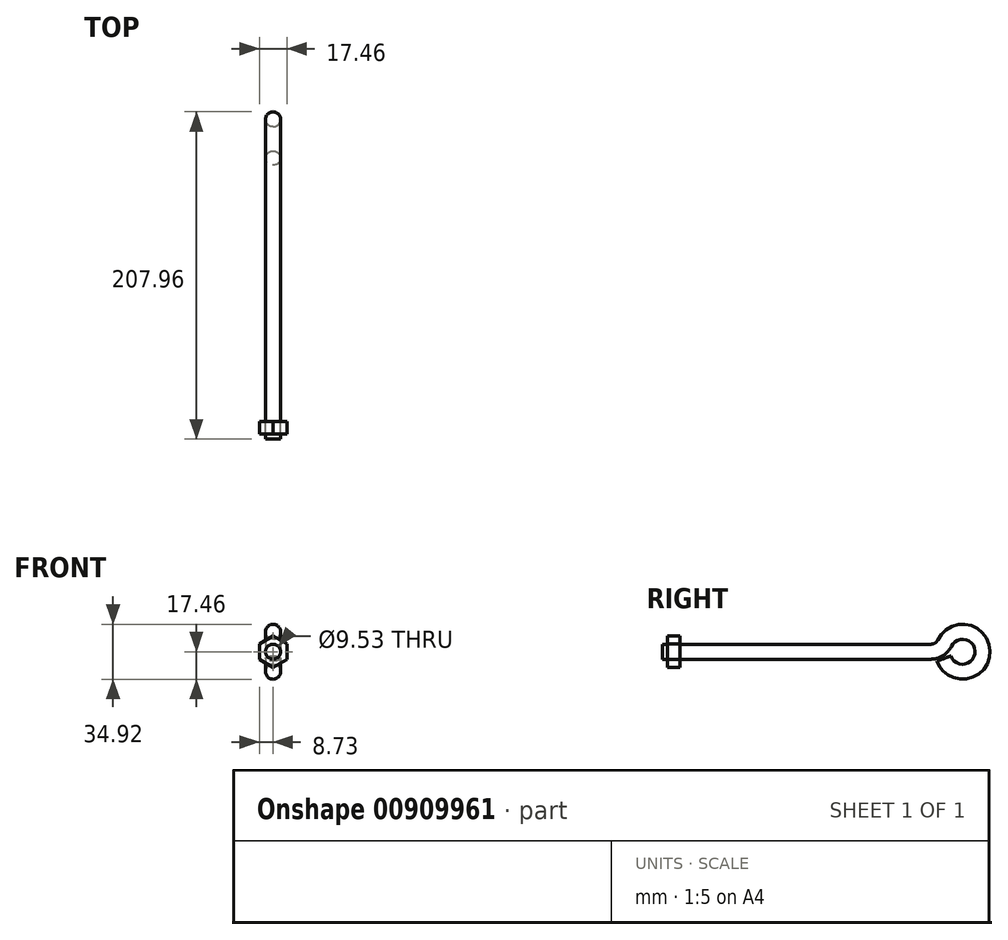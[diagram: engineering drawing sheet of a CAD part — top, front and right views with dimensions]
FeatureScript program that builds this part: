
annotation { "Feature Type Name" : "Feature", "Feature Type Description" : "" }
export const myFeature = defineFeature(function(context is Context, id is Id, definition is map)
    precondition{}
    {
        {
            var Q0;
            Q0=qCreatedBy(makeId("Right.planeOp"),FACE);
            var sketch = newSketch(context, id + "F0", { "sketchPlane" : qUnion([Q0])});
            skLineSegment(sketch, "E0", {"start": v(0, 0) * mm, "end": v(170.42, 0) * mm});
            skArc(sketch, "E1", {"start": v(170.42, 0) * mm, "mid": v(175.51, 1.47) * mm, "end": v(179.03, 5.44) * mm});
            skArc(sketch, "E2", {"start": v(178.57, -4.34) * mm, "mid": v(203.19, -0.6) * mm, "end": v(179.03, 5.44) * mm});
            skLineSegment(sketch, "E3", {"start": v(190.5, 0) * mm, "end": v(178.57, -4.34) * mm, "construction": true});
            skSolve(sketch);
        }
        {
            var Q0;
            Q0=qCreatedBy(makeId("Front.planeOp"),FACE);
            var sketch = newSketch(context, id + "F1", { "sketchPlane" : qUnion([Q0])});
            skCircle(sketch, "E4", {"center": v(0, 0) * mm, "radius": 4.76 * mm});
            skSolve(sketch);
        }
        {
            var Q0;
            Q0=makeQuery(id+"F1.imprint","IMPRINT",FACE,{"disambiguationData":[TD([[makeQuery(id+"F1.imprint","IMPRINT",EDGE,{"derivedFrom":sQuery(id+"F1.wireOp",EDGE,"E4")}),1.0]])]});
            var Q1;
            Q1=sQuery(id+"F0.wireOp",EDGE,"E0");
            var Q2;
            Q2=sQuery(id+"F0.wireOp",EDGE,"E1");
            var Q3;
            Q3=sQuery(id+"F0.wireOp",EDGE,"E2");
            sweep(context, id + "F2", {"profiles" : qUnion([Q0]), "path" : qUnion([Q1, Q2, Q3])});
        }
        {
            var Q0;
            Q0=makeQuery(id+"F2.opSweep","CAP_FACE",FACE,{"disambiguationData":[OSD([sQuery(id+"F0.wireOp",VERTEX,"E0.start"),sQuery(id+"F1.wireOp",EDGE,"E4")])],"isStart":true});
            var sketch = newSketch(context, id + "F3", { "sketchPlane" : qUnion([Q0])});
            skCircle(sketch, "E5.cCircle", {"center": v(0, 0) * mm, "radius": 8.73 * mm, "construction": true});
            skLineSegment(sketch, "E5.0", {"start": v(8.73, 5.04) * mm, "end": v(8.73, -5.04) * mm});
            skLineSegment(sketch, "E5.1", {"start": v(8.73, -5.04) * mm, "end": v(0, -10.08) * mm});
            skLineSegment(sketch, "E5.2", {"start": v(0, -10.08) * mm, "end": v(-8.73, -5.04) * mm});
            skLineSegment(sketch, "E5.3", {"start": v(-8.73, -5.04) * mm, "end": v(-8.73, 5.04) * mm});
            skLineSegment(sketch, "E5.4", {"start": v(-8.73, 5.04) * mm, "end": v(0, 10.08) * mm});
            skLineSegment(sketch, "E5.5", {"start": v(0, 10.08) * mm, "end": v(8.73, 5.04) * mm});
            skPoint(sketch, "E5.0.midPoint", {"position": v(8.73, 0) * mm});
            skSolve(sketch);
        }
        {
            var Q0;
            Q0=makeQuery(id+"F3.imprint","IMPRINT",FACE,{"disambiguationData":[TD([[makeQuery(id+"F3.imprint","IMPRINT",EDGE,{"derivedFrom":sQuery(id+"F3.wireOp",EDGE,"E5.0")}),-1.0]])]});
            extrude(context, id + "F4", {"entities" : qUnion([Q0]), "oppositeDirection" : true, "depth" : 11.1 * mm, "offsetDistance" : 25 * mm});
        }
        {
            var Q0;
            Q0=makeQuery(id+"F4.opExtrude","CAP_FACE",FACE,{"disambiguationData":[OSD([sQuery(id+"F0.wireOp",VERTEX,"E0.start"),sQuery(id+"F1.wireOp",EDGE,"E4"),sQuery(id+"F3.wireOp",EDGE,"E5.0"),sQuery(id+"F3.wireOp",EDGE,"E5.1"),sQuery(id+"F3.wireOp",EDGE,"E5.2"),sQuery(id+"F3.wireOp",EDGE,"E5.3"),sQuery(id+"F3.wireOp",EDGE,"E5.4"),sQuery(id+"F3.wireOp",EDGE,"E5.5")])],"isStart":true});
            extrude(context, id + "F5", {"entities" : qUnion([Q0]), "operationType" : NewBodyOperationType.REMOVE, "oppositeDirection" : true, "depth" : 3.17 * mm, "offsetDistance" : 25 * mm});
        }
    });
